# Revit family: BE_24087_de_DE
name_source: partatom
category: Leuchten
units: mm (PartAtom-declared; Revit-internal decimal feet)

## family parameters
Basisbauteil = Fläche
Beim Laden mit Abzugskörper schneiden = Ja
Bemaßung runder Anschluss = Durchmesser verwenden
Gemeinsam genutzt = Nein
Lichtquelle = Ja
Raumberechnungspunkt = Ja
Teiletyp = Normal

## types (6) — shared parameters
AC/DC = AC/DC
Aktualisierung = 2022-05-18T04:00:07
BEGA_Dummy = Nein
BEGA_IES = Ja
BEGA_Intern = Ja
BEGA_Intern_Konstruktion = Ja
BEGA_Intern_an = Ja
BEGA_Intern_aus = Ja
Befestigungsabstand = 86 x 86 mm
Befestigungsbohrung = Ø 4,5 mm
Beschreibung = Wandleuchte
Beschreibung_Sonderanfertigung = Hier können Sie Informationen zur Sonderanfertigung eintragen.
CE_Konformität = ja
ENEC = ja
Energieeffizienzklasse = LED A++ - A
Farbfilter = 16777215
Farbtemperaturverschiebung bei Dämpfen der Lampe = <Keine Auswahl>
Farbwiedergabeindex = CRI > 80
Frequenz = 0/50-60 Hz
Gewicht = 1.45 kg
Hersteller = BEGA
Lampe = LED 10 W
Lastklassifizierung = Beleuchtung
Lebensdauerkriterien = L70B50 @ 25 °C = 200000 h
Logo = BEGA_Logo.png
Material_02 = BEGA_Oberfläche_Silber_matt
Material_03 = BEGA_Oberfläche_Weiss_matt
Material_06 = BEGA_Oberfläche_Edelstahl_gebürstet
Material_09 = BEGA_Glas_klar
Material_10 = BEGA_Glas_matt
Material_11 = BEGA_Glas_opal
Material_15 = BEGA_Leuchtmedium_matt
Material_17 = BEGA_Reflektor
Neigungswinkel = 0.00°
Produktdatenblatt = https://cdn.bega.com
Scheinlast = 0 VA
Schutzart = IP 65
Schutzklasse = I
Sonderanfertigung = Nein
Spannung = 240 V
Typenbild = 24087.png
URL = https://www.bega.com
Umgebungstemperatur = 25 °C
zero-valued in all types: Vorgabe-Ansicht

## per-type parameters (varying)
| type | Bestellnummer | Datei für fotometrisches Netz | Farbtemperatur | LED_Modulbezeichnung | Lampenlichtstrom | Leuchtenlichtstrom | M_A | M_G | M_W | Modell |
| BEGA_24087_Weiß_K3 | 24087WK3 | BE_24087K3.IES | 3000 K | 2x LED-0887/830 | 1460 lm | 410 lm | Nein | Nein | Ja | 24087WK3 |
| BEGA_24087_Grafit_K4 | 24087K4 | BE_24087K4.IES | 4000 K | 2x LED-0887/840 | 1550 lm | 435 lm | Nein | Ja | Nein | 24087K4 |
| BEGA_24087_Grafit_K3 | 24087K3 | BE_24087K3.IES | 3000 K | 2x LED-0887/830 | 1460 lm | 410 lm | Nein | Ja | Nein | 24087K3 |
| BEGA_24087_Silber_K4 | 24087AK4 | BE_24087K4.IES | 4000 K | 2x LED-0887/840 | 1550 lm | 435 lm | Ja | Nein | Nein | 24087AK4 |
| BEGA_24087_Silber_K3 | 24087AK3 | BE_24087K3.IES | 3000 K | 2x LED-0887/830 | 1460 lm | 410 lm | Ja | Nein | Nein | 24087AK3 |
| BEGA_24087_Weiß_K4 | 24087WK4 | BE_24087K4.IES | 4000 K | 2x LED-0887/840 | 1550 lm | 435 lm | Nein | Nein | Ja | 24087WK4 |
